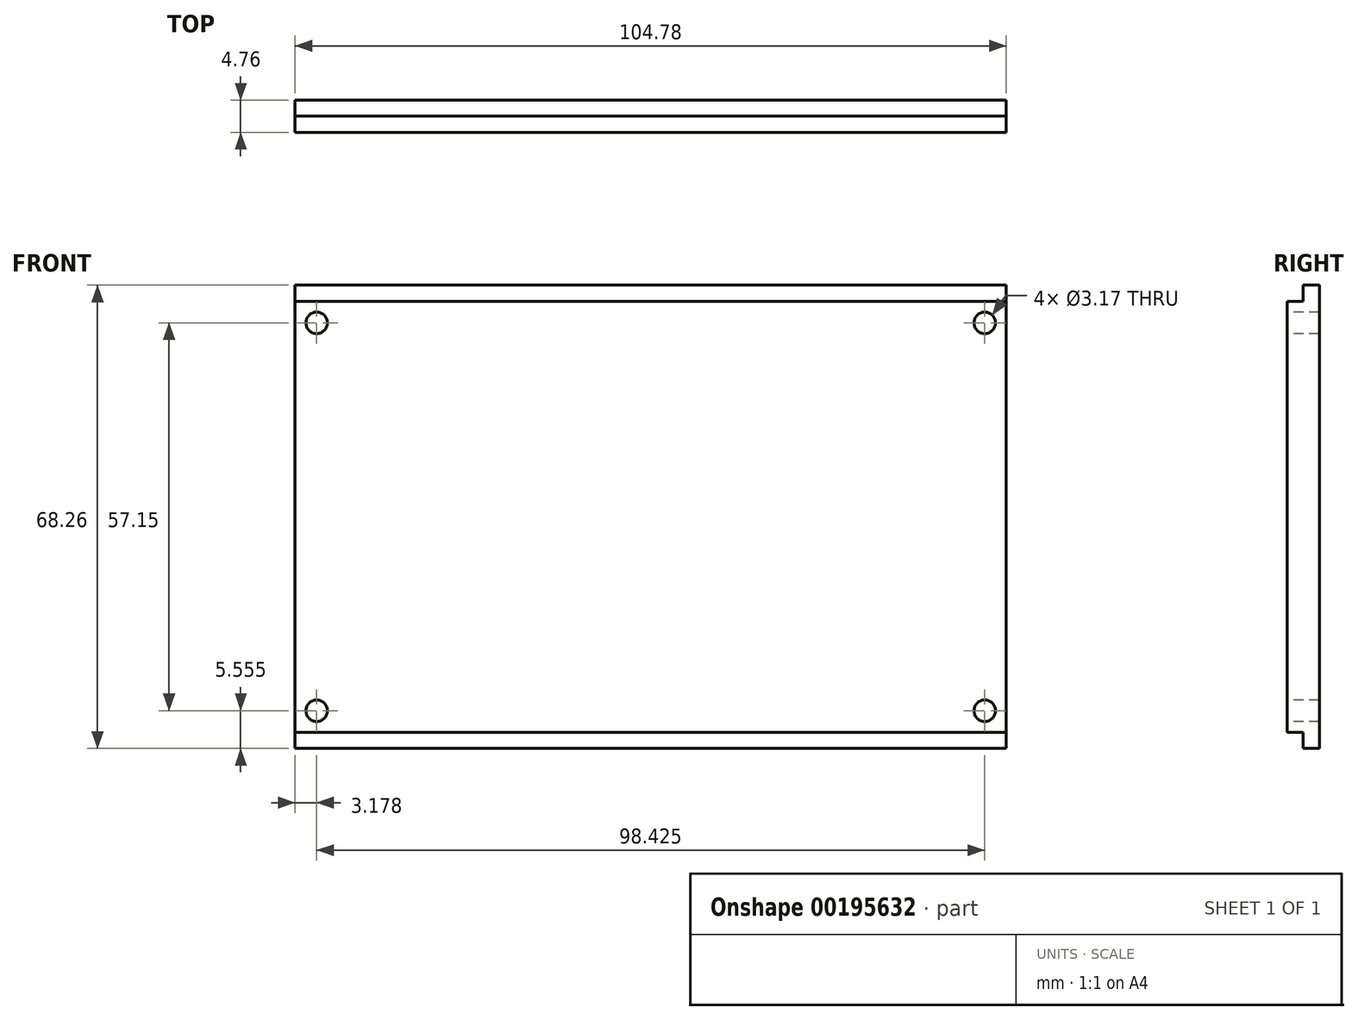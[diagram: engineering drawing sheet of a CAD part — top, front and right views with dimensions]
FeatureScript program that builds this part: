
annotation { "Feature Type Name" : "Feature", "Feature Type Description" : "" }
export const myFeature = defineFeature(function(context is Context, id is Id, definition is map)
    precondition{}
    {
        {
            var Q0;
            Q0=qCreatedBy(makeId("Front.planeOp"),FACE);
            var sketch = newSketch(context, id + "F0", { "sketchPlane" : qUnion([Q0])});
            skLineSegment(sketch, "E0.bottom", {"start": v(-52.39, 34.13) * mm, "end": v(52.39, 34.13) * mm});
            skLineSegment(sketch, "E0.top", {"start": v(-52.39, -34.13) * mm, "end": v(52.39, -34.13) * mm});
            skLineSegment(sketch, "E0.left", {"start": v(-52.39, 34.13) * mm, "end": v(-52.39, -34.13) * mm});
            skLineSegment(sketch, "E0.right", {"start": v(52.39, 34.13) * mm, "end": v(52.39, -34.13) * mm});
            skSolve(sketch);
        }
        {
            var Q0;
            Q0=qSketchRegion(id+"F0",true);
            extrude(context, id + "F1", {"entities" : qUnion([Q0]), "depth" : 4.76 * mm});
        }
        {
            var Q0;
            Q0=makeQuery(id+"F1.opExtrude","SWEPT_FACE",FACE,{"disambiguationData":[OSD([sQuery(id+"F0.wireOp",EDGE,"E0.right")])]});
            var sketch = newSketch(context, id + "F2", { "sketchPlane" : qUnion([Q0])});
            skLineSegment(sketch, "E1.bottom", {"start": v(-4.76, 34.13) * mm, "end": v(-2.38, 34.13) * mm});
            skLineSegment(sketch, "E1.top", {"start": v(-4.76, 31.75) * mm, "end": v(-2.38, 31.75) * mm});
            skLineSegment(sketch, "E1.left", {"start": v(-4.76, 34.13) * mm, "end": v(-4.76, 31.75) * mm});
            skLineSegment(sketch, "E1.right", {"start": v(-2.38, 34.13) * mm, "end": v(-2.38, 31.75) * mm});
            skLineSegment(sketch, "E2.MirrorCS", {"start": v(-4.76, -34.13) * mm, "end": v(-2.38, -34.13) * mm});
            skLineSegment(sketch, "E3.MirrorCS", {"start": v(-4.76, -31.75) * mm, "end": v(-2.38, -31.75) * mm});
            skLineSegment(sketch, "E4.MirrorCS", {"start": v(-4.76, -34.13) * mm, "end": v(-4.76, -31.75) * mm});
            skLineSegment(sketch, "E5.MirrorCS", {"start": v(-2.38, -34.13) * mm, "end": v(-2.38, -31.75) * mm});
            skSolve(sketch);
        }
        {
            var Q0;
            Q0=qSketchRegion(id+"F2",true);
            extrude(context, id + "F3", {"entities" : qUnion([Q0]), "operationType" : NewBodyOperationType.REMOVE, "endBound" : BoundingType.UP_TO_NEXT, "oppositeDirection" : true, "depth" : 25.4 * mm});
        }
        {
            var Q0;
            Q0=makeQuery(id+"F1.opExtrude","CAP_FACE",FACE,{"disambiguationData":[OSD([sQuery(id+"F0.wireOp",EDGE,"E0.bottom"),sQuery(id+"F0.wireOp",EDGE,"E0.top"),sQuery(id+"F0.wireOp",EDGE,"E0.left"),sQuery(id+"F0.wireOp",EDGE,"E0.right")])],"isStart":false});
            var sketch = newSketch(context, id + "F4", { "sketchPlane" : qUnion([Q0])});
            skCircle(sketch, "E6", {"center": v(-49.21, 28.57) * mm, "radius": 1.59 * mm});
            skCircle(sketch, "E7.MirrorC", {"center": v(49.21, 28.57) * mm, "radius": 1.59 * mm});
            skCircle(sketch, "E8.MirrorC", {"center": v(-49.21, -28.57) * mm, "radius": 1.59 * mm});
            skCircle(sketch, "E9.MirrorC", {"center": v(49.21, -28.57) * mm, "radius": 1.59 * mm});
            skSolve(sketch);
        }
        {
            var Q0;
            Q0 = qSketchRegion(id + "F4", true);
            extrude(context, id + "F5", {"entities" : qUnion([Q0]), "operationType" : NewBodyOperationType.REMOVE, "endBound" : BoundingType.UP_TO_NEXT, "oppositeDirection" : true, "depth" : 25.4 * mm});
        }
    });
